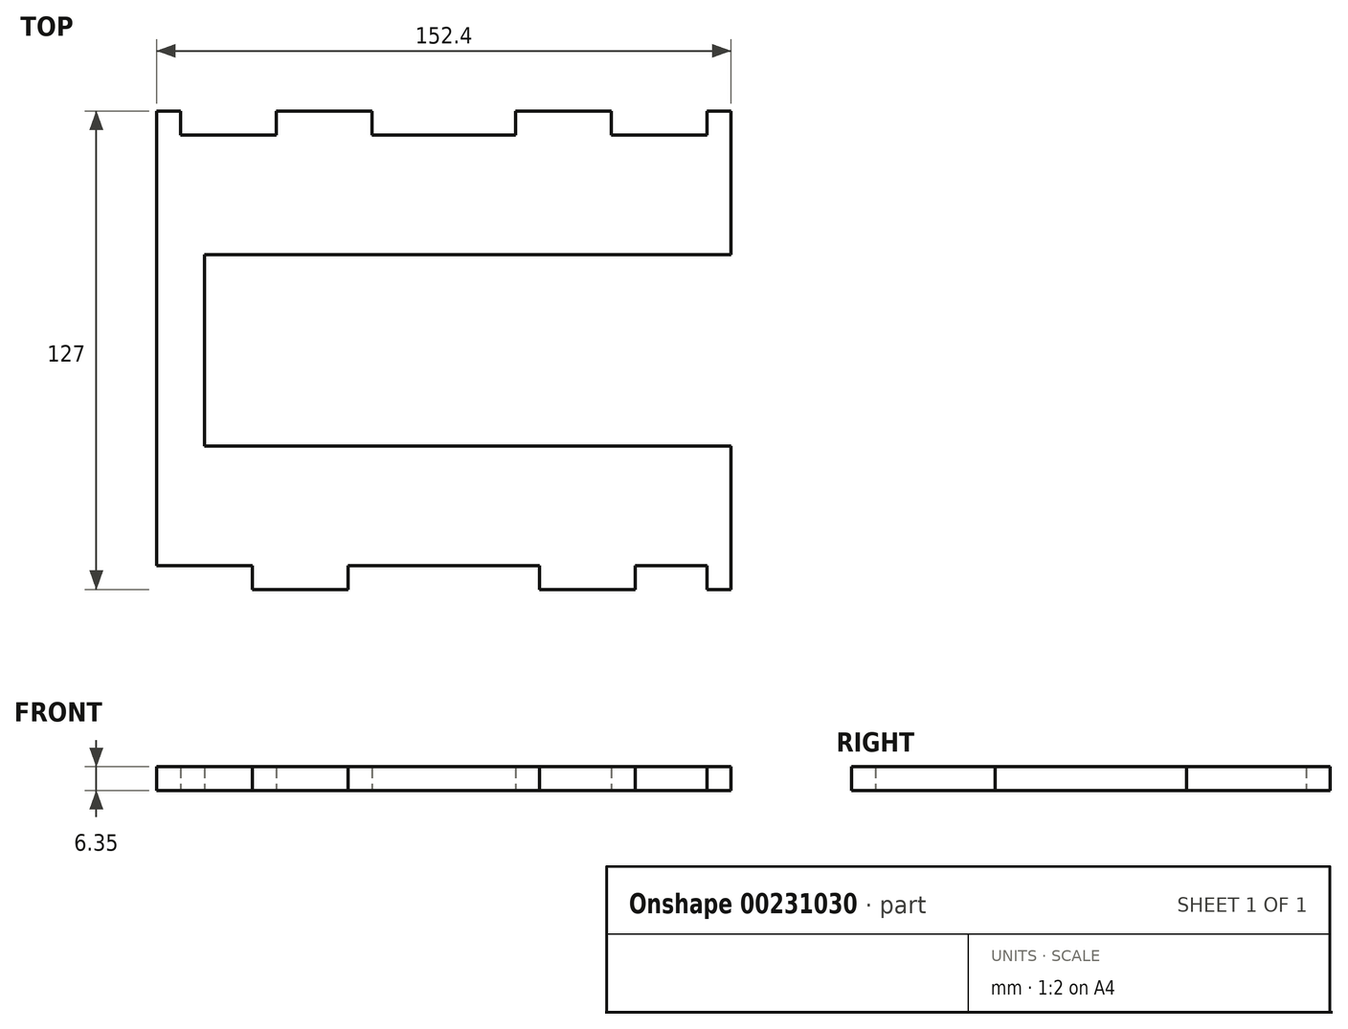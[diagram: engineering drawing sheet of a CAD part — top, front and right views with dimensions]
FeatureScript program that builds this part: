
annotation { "Feature Type Name" : "Feature", "Feature Type Description" : "" }
export const myFeature = defineFeature(function(context is Context, id is Id, definition is map)
    precondition{}
    {
        {
            var Q0;
            Q0=qCreatedBy(makeId("Top.planeOp"),FACE);
            var sketch = newSketch(context, id + "F0", { "sketchPlane" : qUnion([Q0])});
            skLineSegment(sketch, "E0.bottom", {"start": v(76.2, 63.5) * mm, "end": v(69.85, 63.5) * mm});
            skLineSegment(sketch, "E0.top", {"start": v(76.2, -63.5) * mm, "end": v(69.85, -63.5) * mm});
            skLineSegment(sketch, "E0.left", {"start": v(76.2, 63.5) * mm, "end": v(76.2, 50.8) * mm});
            skPoint(sketch, "E0.middle", {"position": v(0, 0) * mm});
            skLineSegment(sketch, "E1", {"start": v(-76.2, -25.4) * mm, "end": v(-69.85, -25.4) * mm});
            skLineSegment(sketch, "E2", {"start": v(-76.2, 25.4) * mm, "end": v(-69.85, 25.4) * mm});
            skLineSegment(sketch, "E3.MirrorCS", {"start": v(69.85, 57.15) * mm, "end": v(63.5, 57.15) * mm});
            skLineSegment(sketch, "E4.MirrorCS", {"start": v(-44.45, 63.5) * mm, "end": v(-44.45, 57.15) * mm});
            skLineSegment(sketch, "E5.MirrorCS", {"start": v(44.45, 63.5) * mm, "end": v(44.45, 57.15) * mm});
            skLineSegment(sketch, "E6.MirrorCS", {"start": v(69.85, 63.5) * mm, "end": v(69.85, 57.15) * mm});
            skLineSegment(sketch, "E7.trimOffspring", {"start": v(76.2, -25.4) * mm, "end": v(76.2, -31.75) * mm});
            skLineSegment(sketch, "E8.trimOffspring", {"start": v(38.1, 63.5) * mm, "end": v(31.75, 63.5) * mm});
            skLineSegment(sketch, "E9.trimOffspring", {"start": v(25.4, 63.5) * mm, "end": v(19.05, 63.5) * mm});
            skLineSegment(sketch, "E10.trimOffspring", {"start": v(-25.4, 63.5) * mm, "end": v(-31.75, 63.5) * mm});
            skLineSegment(sketch, "E11.trimOffspring", {"start": v(-38.1, 63.5) * mm, "end": v(-44.45, 63.5) * mm});
            skPoint(sketch, "E12.MirrorCS.end.orphan", {"position": v(69.85, -63.5) * mm});
            skLineSegment(sketch, "E13.trimOffspring", {"start": v(50.8, -63.5) * mm, "end": v(44.45, -63.5) * mm});
            skLineSegment(sketch, "E14.trimOffspring", {"start": v(38.1, -63.5) * mm, "end": v(31.75, -63.5) * mm});
            skLineSegment(sketch, "E15.trimOffspring", {"start": v(-38.1, -63.5) * mm, "end": v(-44.45, -63.5) * mm});
            skLineSegment(sketch, "E16", {"start": v(-31.75, -63.5) * mm, "end": v(-25.4, -63.5) * mm});
            skLineSegment(sketch, "E17", {"start": v(69.85, -63.5) * mm, "end": v(76.2, -63.5) * mm});
            skLineSegment(sketch, "E18.MirrorCS", {"start": v(-76.2, -50.8) * mm, "end": v(-76.2, -57.15) * mm});
            skLineSegment(sketch, "E19.MirrorCS", {"start": v(-76.2, -44.45) * mm, "end": v(-69.85, -44.45) * mm});
            skLineSegment(sketch, "E20.MirrorCS", {"start": v(-76.2, -38.1) * mm, "end": v(-69.85, -38.1) * mm});
            skLineSegment(sketch, "E21.MirrorCS", {"start": v(-76.2, -31.75) * mm, "end": v(-69.85, -31.75) * mm});
            skLineSegment(sketch, "E22.MirrorCS", {"start": v(-76.2, -6.35) * mm, "end": v(-69.85, -6.35) * mm});
            skLineSegment(sketch, "E23.MirrorCS", {"start": v(-76.2, -12.7) * mm, "end": v(-69.85, -12.7) * mm});
            skLineSegment(sketch, "E24.MirrorCS", {"start": v(-76.2, -19.05) * mm, "end": v(-69.85, -19.05) * mm});
            skLineSegment(sketch, "E25.MirrorCS", {"start": v(-76.2, 6.35) * mm, "end": v(-69.85, 6.35) * mm});
            skLineSegment(sketch, "E26.MirrorCS", {"start": v(-76.2, 0) * mm, "end": v(-69.85, 0) * mm});
            skLineSegment(sketch, "E27.MirrorCS", {"start": v(-76.2, 12.7) * mm, "end": v(-69.85, 12.7) * mm});
            skLineSegment(sketch, "E28.MirrorCS", {"start": v(-76.2, 19.05) * mm, "end": v(-69.85, 19.05) * mm});
            skLineSegment(sketch, "E29.MirrorCS", {"start": v(-76.2, 31.75) * mm, "end": v(-69.85, 31.75) * mm});
            skLineSegment(sketch, "E30.MirrorCS", {"start": v(-76.2, 38.1) * mm, "end": v(-69.85, 38.1) * mm});
            skLineSegment(sketch, "E31.MirrorCS", {"start": v(-76.2, 44.45) * mm, "end": v(-69.85, 44.45) * mm});
            skLineSegment(sketch, "E32", {"start": v(-76.2, -50.8) * mm, "end": v(-69.85, -50.8) * mm});
            skLineSegment(sketch, "E33.trimOffspring", {"start": v(-76.2, -38.1) * mm, "end": v(-76.2, -44.45) * mm});
            skLineSegment(sketch, "E34.trimOffspring", {"start": v(-76.2, -25.4) * mm, "end": v(-76.2, -31.75) * mm});
            skLineSegment(sketch, "E35.trimOffspring", {"start": v(-76.2, -12.7) * mm, "end": v(-76.2, -19.05) * mm});
            skLineSegment(sketch, "E36.trimOffspring", {"start": v(-76.2, 0) * mm, "end": v(-76.2, -6.35) * mm});
            skLineSegment(sketch, "E37.trimOffspring", {"start": v(-76.2, 12.7) * mm, "end": v(-76.2, 6.35) * mm});
            skLineSegment(sketch, "E38.trimOffspring", {"start": v(-76.2, 25.4) * mm, "end": v(-76.2, 19.05) * mm});
            skLineSegment(sketch, "E39.trimOffspring", {"start": v(-76.2, 38.1) * mm, "end": v(-76.2, 31.75) * mm});
            skLineSegment(sketch, "E40.trimOffspring", {"start": v(-76.2, 50.8) * mm, "end": v(-76.2, 44.45) * mm});
            skLineSegment(sketch, "E41.trimOffspring", {"start": v(76.2, -50.8) * mm, "end": v(76.2, -63.5) * mm});
            skLineSegment(sketch, "E42.trimOffspring", {"start": v(76.2, -38.1) * mm, "end": v(76.2, -44.45) * mm});
            skLineSegment(sketch, "E43.trimOffspring", {"start": v(76.2, 44.45) * mm, "end": v(76.2, 38.1) * mm});
            skLineSegment(sketch, "E44.trimOffspring", {"start": v(76.2, 31.75) * mm, "end": v(76.2, 25.4) * mm});
            skLineSegment(sketch, "E45.right", {"start": v(76.2, -38.1) * mm, "end": v(76.2, -31.75) * mm});
            skLineSegment(sketch, "E46.right", {"start": v(76.2, 31.75) * mm, "end": v(76.2, 38.1) * mm});
            skLineSegment(sketch, "E47.trimOffspring", {"start": v(-63.5, -25.4) * mm, "end": v(-63.5, 25.4) * mm});
            skLineSegment(sketch, "E48.trimOffspring", {"start": v(-6.35, -57.15) * mm, "end": v(-12.7, -57.15) * mm});
            skLineSegment(sketch, "E49.trimOffspring", {"start": v(6.35, -57.15) * mm, "end": v(0, -57.15) * mm});
            skLineSegment(sketch, "E50.trimOffspring", {"start": v(19.05, -57.15) * mm, "end": v(12.7, -57.15) * mm});
            skPoint(sketch, "E51.orphan", {"position": v(76.2, -57.15) * mm});
            skLineSegment(sketch, "E52.trimOffspring", {"start": v(-69.85, -50.8) * mm, "end": v(-69.85, -44.45) * mm});
            skLineSegment(sketch, "E53.trimOffspring", {"start": v(-69.85, -38.1) * mm, "end": v(-69.85, -31.75) * mm});
            skLineSegment(sketch, "E54.trimOffspring", {"start": v(-69.85, -25.4) * mm, "end": v(-69.85, -19.05) * mm});
            skLineSegment(sketch, "E55.trimOffspring", {"start": v(-63.5, -25.4) * mm, "end": v(76.2, -25.4) * mm});
            skLineSegment(sketch, "E56.trimOffspring", {"start": v(-69.85, -12.7) * mm, "end": v(-69.85, -6.35) * mm});
            skLineSegment(sketch, "E57.trimOffspring", {"start": v(-69.85, 0) * mm, "end": v(-69.85, 6.35) * mm});
            skLineSegment(sketch, "E58.trimOffspring", {"start": v(-69.85, 12.7) * mm, "end": v(-69.85, 19.05) * mm});
            skLineSegment(sketch, "E59.trimOffspring", {"start": v(-69.85, 25.4) * mm, "end": v(-69.85, 31.75) * mm});
            skLineSegment(sketch, "E60.trimOffspring", {"start": v(-69.85, 38.1) * mm, "end": v(-69.85, 44.45) * mm});
            skLineSegment(sketch, "E61.trimOffspring", {"start": v(-63.5, 25.4) * mm, "end": v(76.2, 25.4) * mm});
            skPoint(sketch, "E62.orphan", {"position": v(-69.85, 63.5) * mm});
            skLineSegment(sketch, "E63.trimOffspring", {"start": v(57.15, 57.15) * mm, "end": v(50.8, 57.15) * mm});
            skLineSegment(sketch, "E64.trimOffspring", {"start": v(69.85, 57.15) * mm, "end": v(69.85, 63.5) * mm});
            skLineSegment(sketch, "E65", {"start": v(-38.1, 63.5) * mm, "end": v(-31.75, 63.5) * mm});
            skLineSegment(sketch, "E66", {"start": v(-25.4, 63.5) * mm, "end": v(-19.05, 63.5) * mm});
            skLineSegment(sketch, "E67", {"start": v(25.4, 63.5) * mm, "end": v(31.75, 63.5) * mm});
            skLineSegment(sketch, "E68", {"start": v(38.1, 63.5) * mm, "end": v(44.45, 63.5) * mm});
            skLineSegment(sketch, "E69", {"start": v(-69.85, 63.5) * mm, "end": v(-69.85, 57.15) * mm});
            skLineSegment(sketch, "E70.bottom", {"start": v(-69.85, 63.5) * mm, "end": v(-76.2, 63.5) * mm});
            skLineSegment(sketch, "E70.right", {"start": v(-76.2, 63.5) * mm, "end": v(-76.2, 50.8) * mm});
            skLineSegment(sketch, "E71", {"start": v(-69.85, 57.15) * mm, "end": v(-44.45, 57.15) * mm});
            skLineSegment(sketch, "E72", {"start": v(57.15, 57.15) * mm, "end": v(63.5, 57.15) * mm});
            skLineSegment(sketch, "E73", {"start": v(44.45, 57.15) * mm, "end": v(50.8, 57.15) * mm});
            skLineSegment(sketch, "E74", {"start": v(-12.7, -57.15) * mm, "end": v(0, -57.15) * mm});
            skLineSegment(sketch, "E75", {"start": v(12.7, -57.15) * mm, "end": v(6.35, -57.15) * mm});
            skLineSegment(sketch, "E76", {"start": v(25.4, -63.5) * mm, "end": v(50.8, -63.5) * mm});
            skLineSegment(sketch, "E77.MirrorCS", {"start": v(-19.05, -57.15) * mm, "end": v(-12.7, -57.15) * mm});
            skLineSegment(sketch, "E78", {"start": v(-69.85, -57.15) * mm, "end": v(-50.8, -57.15) * mm});
            skLineSegment(sketch, "E79", {"start": v(-50.8, -57.15) * mm, "end": v(-50.8, -63.5) * mm});
            skLineSegment(sketch, "E80.trimOffspring", {"start": v(-50.8, -63.5) * mm, "end": v(-31.75, -63.5) * mm});
            skLineSegment(sketch, "E81", {"start": v(-19.05, -57.15) * mm, "end": v(-25.4, -57.15) * mm});
            skLineSegment(sketch, "E82", {"start": v(-25.4, -57.15) * mm, "end": v(-25.4, -63.5) * mm});
            skLineSegment(sketch, "E83.MirrorCS", {"start": v(25.4, -57.15) * mm, "end": v(19.05, -57.15) * mm});
            skLineSegment(sketch, "E84.MirrorCS", {"start": v(25.4, -63.5) * mm, "end": v(25.4, -57.15) * mm});
            skLineSegment(sketch, "E85", {"start": v(69.85, -57.15) * mm, "end": v(57.15, -57.15) * mm});
            skLineSegment(sketch, "E86", {"start": v(57.15, -57.15) * mm, "end": v(50.8, -57.15) * mm});
            skLineSegment(sketch, "E87", {"start": v(50.8, -57.15) * mm, "end": v(50.8, -63.5) * mm});
            skLineSegment(sketch, "E88", {"start": v(69.85, -63.5) * mm, "end": v(69.85, -57.15) * mm});
            skLineSegment(sketch, "E89", {"start": v(-69.85, -57.15) * mm, "end": v(-76.2, -57.15) * mm});
            skLineSegment(sketch, "E90", {"start": v(76.2, -50.8) * mm, "end": v(76.2, -44.45) * mm});
            skLineSegment(sketch, "E91", {"start": v(-76.2, -50.8) * mm, "end": v(-76.2, -44.45) * mm});
            skLineSegment(sketch, "E92", {"start": v(-76.2, -38.1) * mm, "end": v(-76.2, -31.75) * mm});
            skLineSegment(sketch, "E93", {"start": v(-76.2, -25.4) * mm, "end": v(-76.2, -19.05) * mm});
            skLineSegment(sketch, "E94", {"start": v(-76.2, -12.7) * mm, "end": v(-76.2, -6.35) * mm});
            skLineSegment(sketch, "E95", {"start": v(-76.2, 0) * mm, "end": v(-76.2, 6.35) * mm});
            skLineSegment(sketch, "E96", {"start": v(-76.2, 12.7) * mm, "end": v(-76.2, 19.05) * mm});
            skLineSegment(sketch, "E97", {"start": v(-76.2, 25.4) * mm, "end": v(-76.2, 31.75) * mm});
            skLineSegment(sketch, "E98", {"start": v(-76.2, 38.1) * mm, "end": v(-76.2, 44.45) * mm});
            skLineSegment(sketch, "E99", {"start": v(-19.05, 63.5) * mm, "end": v(-19.05, 57.15) * mm});
            skLineSegment(sketch, "E100", {"start": v(-19.05, 57.15) * mm, "end": v(19.05, 57.15) * mm});
            skLineSegment(sketch, "E101", {"start": v(19.05, 57.15) * mm, "end": v(19.05, 63.5) * mm});
            skLineSegment(sketch, "E102", {"start": v(76.2, 44.45) * mm, "end": v(76.2, 50.8) * mm});
            skSolve(sketch);
        }
        {
            var Q0;
            Q0 = qSketchRegion(id + "F0", true);
            extrude(context, id + "F1", {"entities" : qUnion([Q0]), "depth" : 6.35 * mm});
        }
    });
